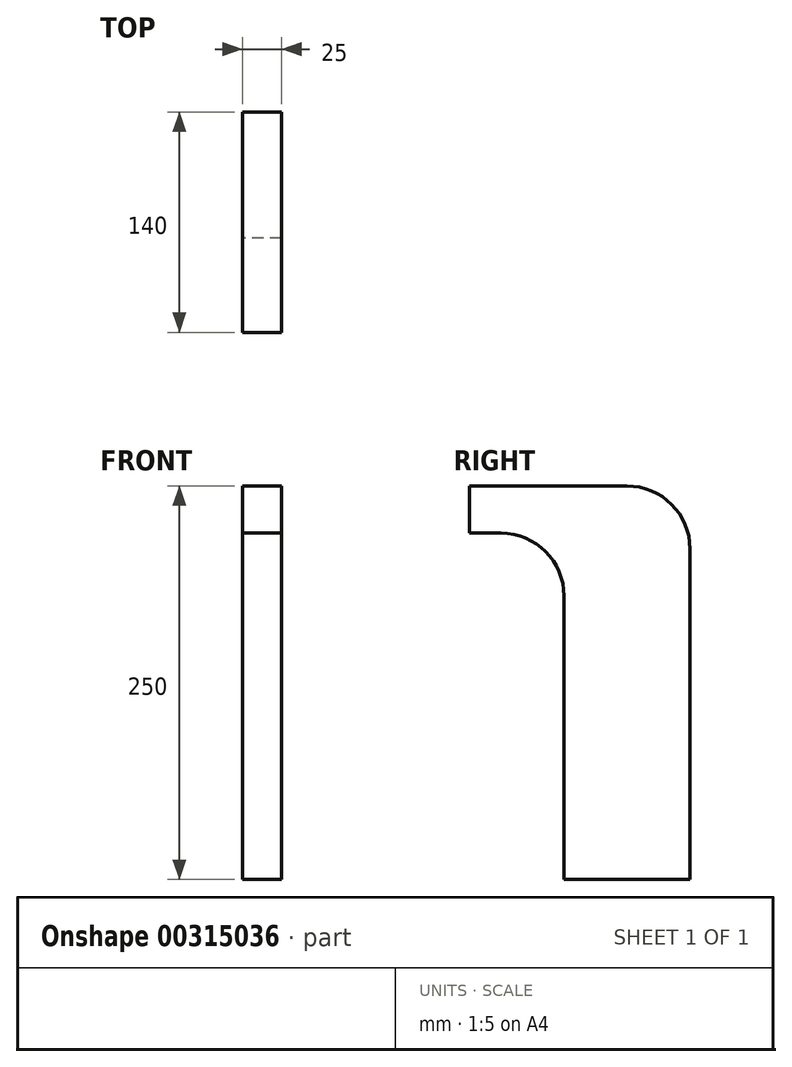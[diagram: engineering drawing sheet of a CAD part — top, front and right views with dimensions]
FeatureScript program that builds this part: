
annotation { "Feature Type Name" : "Feature", "Feature Type Description" : "" }
export const myFeature = defineFeature(function(context is Context, id is Id, definition is map)
    precondition{}
    {
        {
            var Q0;
            Q0=qCreatedBy(makeId("Right.planeOp"),FACE);
            var sketch = newSketch(context, id + "F0", { "sketchPlane" : qUnion([Q0])});
            skLineSegment(sketch, "E0", {"start": v(0, 0) * mm, "end": v(80, 0) * mm});
            skLineSegment(sketch, "E1", {"start": v(0, 0) * mm, "end": v(0, 180) * mm});
            skLineSegment(sketch, "E2", {"start": v(80, 0) * mm, "end": v(80, 210) * mm});
            skLineSegment(sketch, "E3", {"start": v(0, 0) * mm, "end": v(-60, 0) * mm, "construction": true});
            skLineSegment(sketch, "E4", {"start": v(-60, 0) * mm, "end": v(-60, 250) * mm, "construction": true});
            skLineSegment(sketch, "E5.bottom", {"start": v(-60, 250) * mm, "end": v(40, 250) * mm});
            skLineSegment(sketch, "E5.top", {"start": v(-60, 220) * mm, "end": v(-40, 220) * mm});
            skLineSegment(sketch, "E5.left", {"start": v(-60, 250) * mm, "end": v(-60, 220) * mm});
            skPoint(sketch, "E6.visualSharp", {"position": v(80, 250) * mm});
            skArc(sketch, "E6.filletArc", {"start": v(80, 210) * mm, "mid": v(68.28, 238.28) * mm, "end": v(40, 250) * mm});
            skPoint(sketch, "E7.visualSharp", {"position": v(0, 220) * mm});
            skArc(sketch, "E7.filletArc", {"start": v(0, 180) * mm, "mid": v(-11.72, 208.28) * mm, "end": v(-40, 220) * mm});
            skSolve(sketch);
        }
        {
            var Q0;
            Q0=makeQuery(id+"F0.imprint","IMPRINT",FACE,{"disambiguationData":[TD([[makeQuery(id+"F0.imprint","IMPRINT",EDGE,{"derivedFrom":sQuery(id+"F0.wireOp",EDGE,"E0")}),1.0]])]});
            extrude(context, id + "F1", {"entities" : qUnion([Q0]), "endBound" : BoundingType.SYMMETRIC, "depth" : 25 * mm});
        }
    });
